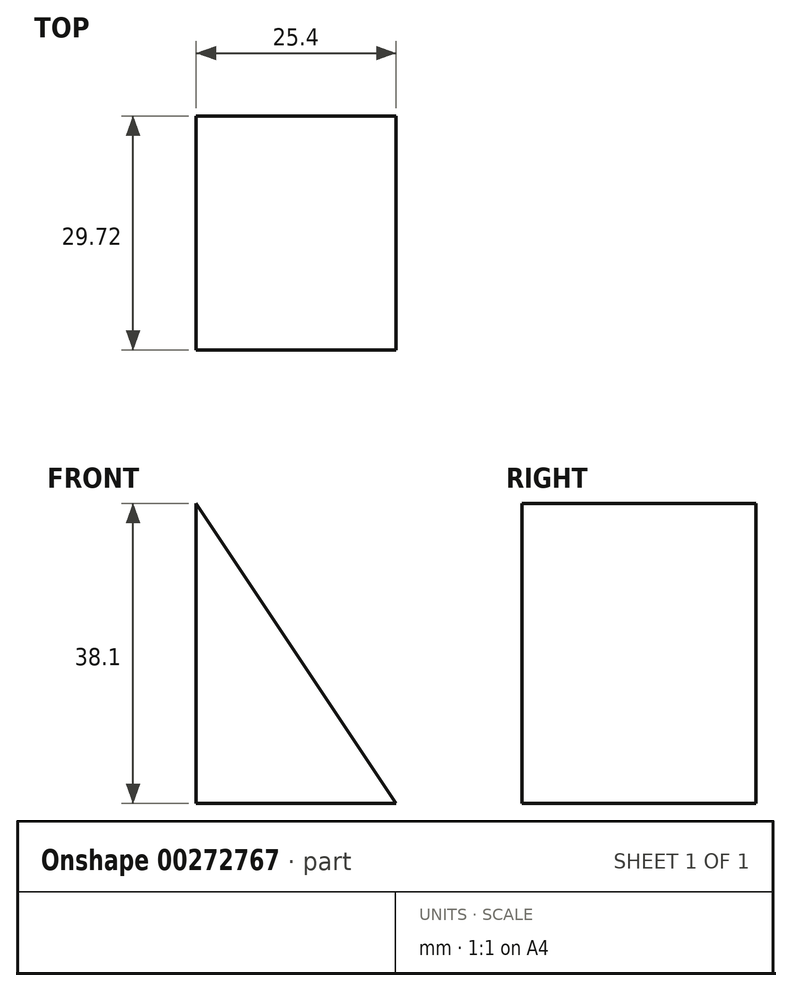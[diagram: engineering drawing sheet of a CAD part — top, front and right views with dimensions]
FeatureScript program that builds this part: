
annotation { "Feature Type Name" : "Feature", "Feature Type Description" : "" }
export const myFeature = defineFeature(function(context is Context, id is Id, definition is map)
    precondition{}
    {
        {
            var Q0;
            Q0=qCreatedBy(makeId("Front.planeOp"),FACE);
            var sketch = newSketch(context, id + "F0", { "sketchPlane" : qUnion([Q0])});
            skLineSegment(sketch, "E0", {"start": v(0, 0) * mm, "end": v(-25.4, 0) * mm});
            skLineSegment(sketch, "E1", {"start": v(-25.4, 0) * mm, "end": v(-25.4, 38.1) * mm});
            skLineSegment(sketch, "E2", {"start": v(-25.4, 38.1) * mm, "end": v(0, 0) * mm});
            skSolve(sketch);
        }
        {
            var Q0;
            Q0 = qSketchRegion(id + "F0", true);
            extrude(context, id + "F1", {"entities" : qUnion([Q0]), "depth" : 29.72 * mm});
        }
    });
